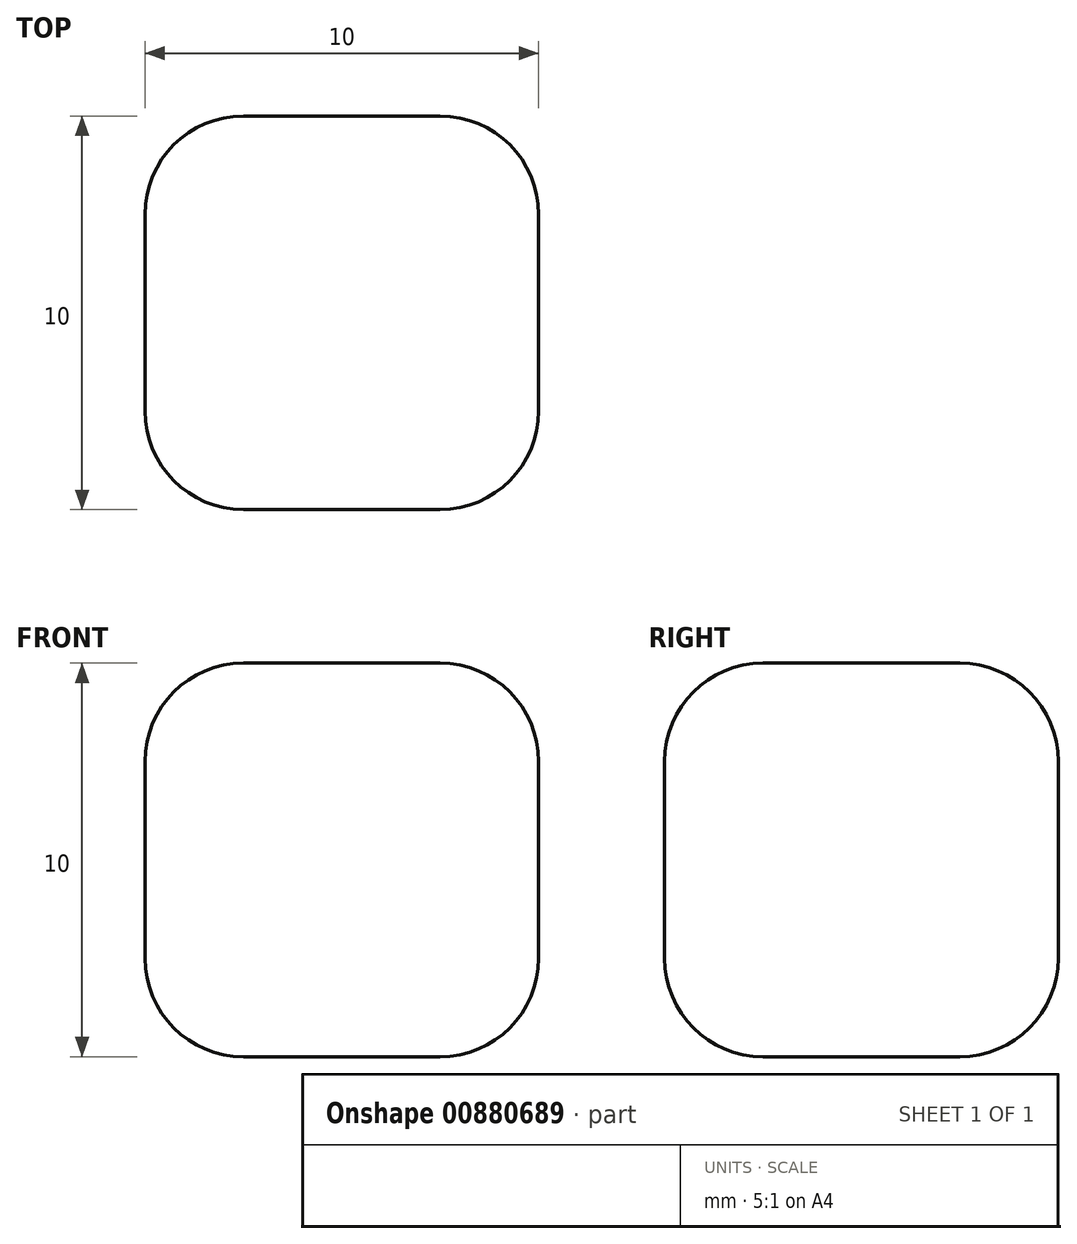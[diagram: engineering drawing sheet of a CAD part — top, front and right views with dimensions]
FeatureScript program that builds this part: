
annotation { "Feature Type Name" : "Feature", "Feature Type Description" : "" }
export const myFeature = defineFeature(function(context is Context, id is Id, definition is map)
    precondition{}
    {
        {
            assignVariable(context, id + "F0", {"name" : "height", "anyValue" : 10});
        }
        {
            var Q0;
            Q0=qCreatedBy(makeId("Front.planeOp"),FACE);
            var sketch = newSketch(context, id + "F1", { "sketchPlane" : qUnion([Q0])});
            skLineSegment(sketch, "E0", {"start": v(-5, 5) * mm, "end": v(5, 5) * mm});
            skLineSegment(sketch, "E1", {"start": v(5, 5) * mm, "end": v(5, -5) * mm});
            skLineSegment(sketch, "E2", {"start": v(5, -5) * mm, "end": v(-5, -5) * mm});
            skLineSegment(sketch, "E3", {"start": v(-5, -5) * mm, "end": v(-5, 5) * mm});
            skSolve(sketch);
        }
        {
            var Q0;
            Q0=makeQuery(id+"F1.imprint","IMPRINT",FACE,{"disambiguationData":[TD([[makeQuery(id+"F1.imprint","IMPRINT",EDGE,{"derivedFrom":sQuery(id+"F1.wireOp",EDGE,"E0")}),-1.0]])]});
            extrude(context, id + "F2", {"entities" : qUnion([Q0]), "endBound" : BoundingType.SYMMETRIC, "depth" : (getVariable(context, 'height')) * mm, "offsetDistance" : 25 * mm});
        }
        {
            var Q0;
            Q0=makeQuery(id+"F2.opExtrude","SWEPT_EDGE",EDGE,{"disambiguationData":[OSD([sQuery(id+"F1.wireOp",EDGE,"E0"),sQuery(id+"F1.wireOp",EDGE,"E1")])]});
            var Q1;
            Q1=makeQuery(id+"F2.opExtrude","SWEPT_EDGE",EDGE,{"disambiguationData":[OSD([sQuery(id+"F1.wireOp",EDGE,"E2"),sQuery(id+"F1.wireOp",EDGE,"E3")])]});
            var Q2;
            Q2=makeQuery(id+"F2.opExtrude","SWEPT_EDGE",EDGE,{"disambiguationData":[OSD([sQuery(id+"F1.wireOp",EDGE,"E0"),sQuery(id+"F1.wireOp",EDGE,"E3")])]});
            var Q3;
            Q3=makeQuery(id+"F2.opExtrude","CAP_EDGE",EDGE,{"disambiguationData":[OSD([sQuery(id+"F1.wireOp",EDGE,"E1")])],"isStart":true});
            var Q4;
            Q4=makeQuery(id+"F2.opExtrude","CAP_EDGE",EDGE,{"disambiguationData":[OSD([sQuery(id+"F1.wireOp",EDGE,"E0")])],"isStart":true});
            var Q5;
            Q5=makeQuery(id+"F2.opExtrude","CAP_EDGE",EDGE,{"disambiguationData":[OSD([sQuery(id+"F1.wireOp",EDGE,"E3")])],"isStart":true});
            var Q6;
            Q6=makeQuery(id+"F2.opExtrude","CAP_EDGE",EDGE,{"disambiguationData":[OSD([sQuery(id+"F1.wireOp",EDGE,"E2")])],"isStart":true});
            var Q7;
            Q7=makeQuery(id+"F2.opExtrude","CAP_EDGE",EDGE,{"disambiguationData":[OSD([sQuery(id+"F1.wireOp",EDGE,"E3")])],"isStart":false});
            var Q8;
            Q8=makeQuery(id+"F2.opExtrude","CAP_EDGE",EDGE,{"disambiguationData":[OSD([sQuery(id+"F1.wireOp",EDGE,"E0")])],"isStart":false});
            var Q9;
            Q9=makeQuery(id+"F2.opExtrude","CAP_EDGE",EDGE,{"disambiguationData":[OSD([sQuery(id+"F1.wireOp",EDGE,"E1")])],"isStart":false});
            var Q10;
            Q10=makeQuery(id+"F2.opExtrude","CAP_EDGE",EDGE,{"disambiguationData":[OSD([sQuery(id+"F1.wireOp",EDGE,"E2")])],"isStart":false});
            var Q11;
            Q11=makeQuery(id+"F2.opExtrude","SWEPT_EDGE",EDGE,{"disambiguationData":[OSD([sQuery(id+"F1.wireOp",EDGE,"E1"),sQuery(id+"F1.wireOp",EDGE,"E2")])]});
            fillet(context, id + "F3", {"entities" : qUnion([Q0, Q1, Q2, Q3, Q4, Q5, Q6, Q7, Q8, Q9, Q10, Q11]), "radius" : getVariable(context, 'height') / 4 * mm, "tangentPropagation" : true, "allowEdgeOverflow" : false});
        }
    });
